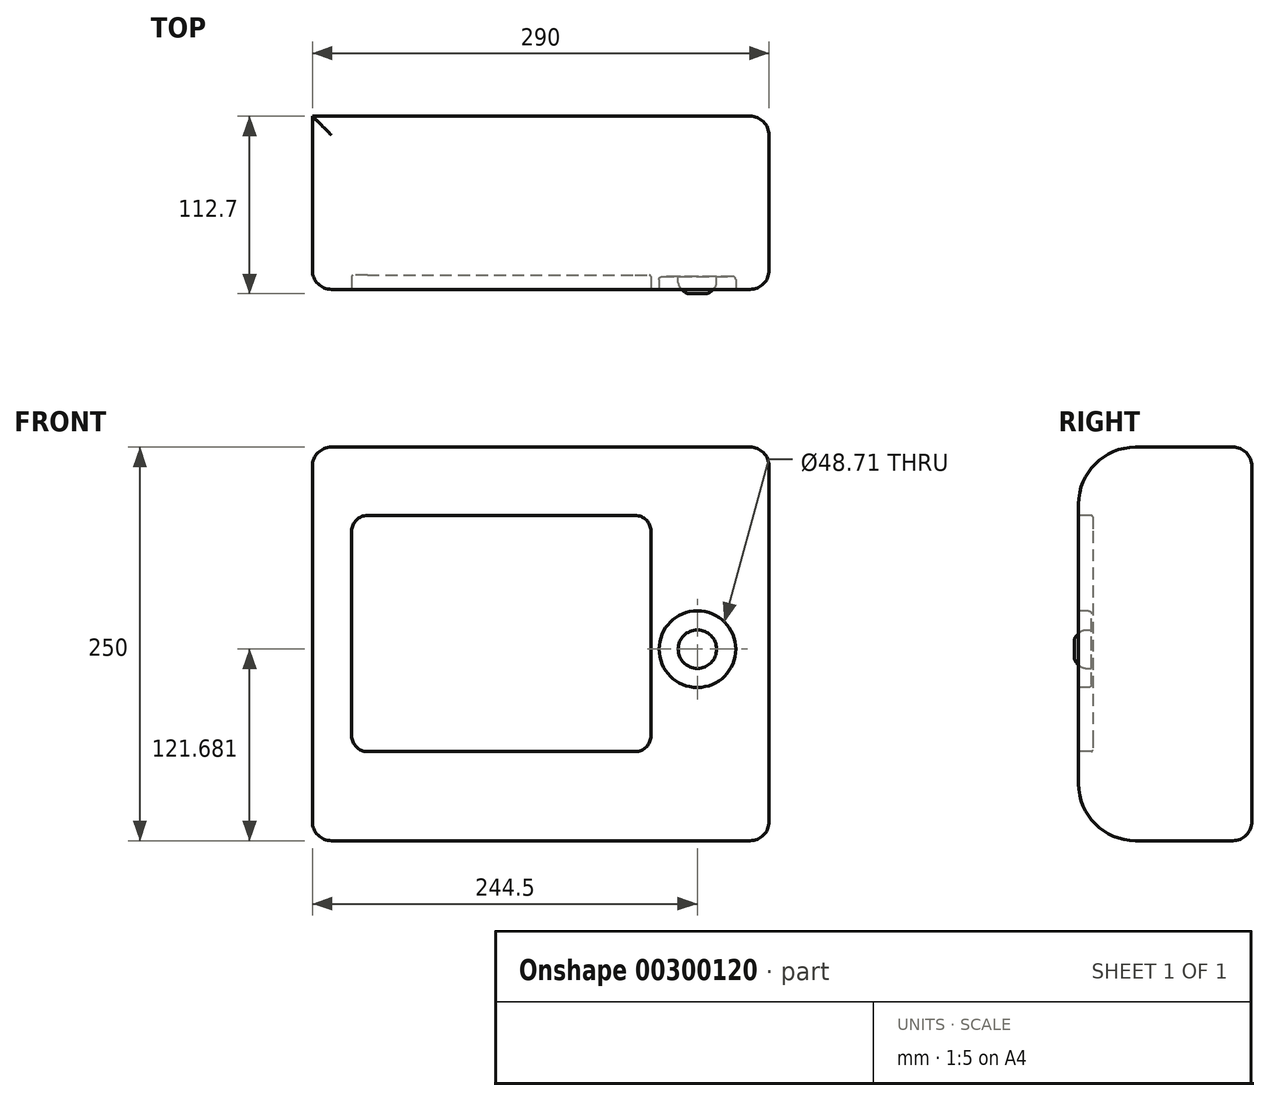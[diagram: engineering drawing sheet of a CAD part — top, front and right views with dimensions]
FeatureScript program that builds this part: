
annotation { "Feature Type Name" : "Feature", "Feature Type Description" : "" }
export const myFeature = defineFeature(function(context is Context, id is Id, definition is map)
    precondition{}
    {
        {
            var Q0;
            Q0=qCreatedBy(makeId("Front.planeOp"),FACE);
            var sketch = newSketch(context, id + "F0", { "sketchPlane" : qUnion([Q0])});
            skLineSegment(sketch, "E0.bottom", {"start": v(-138.87, -70.81) * mm, "end": v(151.13, -70.81) * mm});
            skLineSegment(sketch, "E0.top", {"start": v(-138.87, 179.19) * mm, "end": v(151.13, 179.19) * mm});
            skLineSegment(sketch, "E0.left", {"start": v(-138.87, -70.81) * mm, "end": v(-138.87, 179.19) * mm});
            skLineSegment(sketch, "E0.right", {"start": v(151.13, -70.81) * mm, "end": v(151.13, 179.19) * mm});
            skSolve(sketch);
        }
        {
            var Q0;
            Q0 = qSketchRegion(id + "F0", true);
            extrude(context, id + "F1", {"entities" : qUnion([Q0]), "depth" : 110 * mm});
        }
        {
            var Q0;
            Q0=makeQuery(id+"F1.opExtrude","CAP_EDGE",EDGE,{"disambiguationData":[OSD([sQuery(id+"F0.wireOp",EDGE,"E0.top")])],"isStart":false});
            var Q1;
            Q1=makeQuery(id+"F1.opExtrude","CAP_EDGE",EDGE,{"disambiguationData":[OSD([sQuery(id+"F0.wireOp",EDGE,"E0.bottom")])],"isStart":false});
            fillet(context, id + "F2", {"entities" : qUnion([Q0, Q1]), "radius" : 36.2 * mm, "tangentPropagation" : true, "allowEdgeOverflow" : false});
        }
        {
            var Q0;
            Q0=makeQuery(id+"F1.opExtrude","SWEPT_EDGE",EDGE,{"disambiguationData":[OSD([sQuery(id+"F0.wireOp",EDGE,"E0.top"),sQuery(id+"F0.wireOp",EDGE,"E0.right")])]});
            var Q1;
            Q1=makeQuery(id+"F2.opFillet","BLEND_EDGE",EDGE,{"blendedFrom":[makeQuery(id+"F1.opExtrude","CAP_EDGE",EDGE,{"disambiguationData":[OSD([sQuery(id+"F0.wireOp",EDGE,"E0.top")])],"isStart":false}),makeQuery(id+"F1.opExtrude","SWEPT_FACE",FACE,{"disambiguationData":[OSD([sQuery(id+"F0.wireOp",EDGE,"E0.left")])]})],"blendedInto":[makeQuery(id+"F1.opExtrude","SWEPT_FACE",FACE,{"disambiguationData":[OSD([sQuery(id+"F0.wireOp",EDGE,"E0.left")])]})]});
            var Q2;
            Q2=makeQuery(id+"F1.opExtrude","CAP_EDGE",EDGE,{"disambiguationData":[OSD([sQuery(id+"F0.wireOp",EDGE,"E0.top")])],"isStart":true});
            var Q3;
            Q3=makeQuery(id+"F1.opExtrude","CAP_EDGE",EDGE,{"disambiguationData":[OSD([sQuery(id+"F0.wireOp",EDGE,"E0.right")])],"isStart":true});
            var Q4;
            Q4=makeQuery(id+"F1.opExtrude","CAP_EDGE",EDGE,{"disambiguationData":[OSD([sQuery(id+"F0.wireOp",EDGE,"E0.bottom")])],"isStart":true});
            fillet(context, id + "F3", {"entities" : qUnion([Q0, Q1, Q2, Q3, Q4]), "radius" : 12.07 * mm, "tangentPropagation" : true, "allowEdgeOverflow" : false});
        }
        {
            var Q0;
            Q0=makeQuery(id+"F1.opExtrude","CAP_FACE",FACE,{"disambiguationData":[OSD([sQuery(id+"F0.wireOp",EDGE,"E0.bottom"),sQuery(id+"F0.wireOp",EDGE,"E0.top"),sQuery(id+"F0.wireOp",EDGE,"E0.left"),sQuery(id+"F0.wireOp",EDGE,"E0.right")])],"isStart":false});
            var sketch = newSketch(context, id + "F4", { "sketchPlane" : qUnion([Q0])});
            skCircle(sketch, "E1", {"center": v(105.63, 50.87) * mm, "radius": 24.36 * mm});
            skSolve(sketch);
        }
        {
            var Q0;
            Q0=makeQuery(id+"F4.imprint","IMPRINT",FACE,{"disambiguationData":[TD([[makeQuery(id+"F4.imprint","IMPRINT",EDGE,{"derivedFrom":sQuery(id+"F4.wireOp",EDGE,"E1")}),1.0]])]});
            var Q1;
            Q1=sQuery(id+"F4.wireOp",EDGE,"E1");
            extrude(context, id + "F5", {"entities" : qUnion([Q0]), "operationType" : NewBodyOperationType.REMOVE, "surfaceEntities" : qUnion([Q1]), "oppositeDirection" : true, "depth" : 8.2 * mm});
        }
        {
            var Q0;
            Q0=makeQuery(id+"F5.boolean.opBoolean","COPY",FACE,{"derivedFrom":makeQuery(id+"F5.opExtrude","CAP_FACE",FACE,{"disambiguationData":[OSD([sQuery(id+"F4.wireOp",EDGE,"E1")])],"isStart":false})});
            var sketch = newSketch(context, id + "F6", { "sketchPlane" : qUnion([Q0])});
            skCircle(sketch, "E2", {"center": v(105.63, 50.87) * mm, "radius": 12.21 * mm});
            skSolve(sketch);
        }
        {
            var Q0;
            Q0 = qSketchRegion(id + "F6", true);
            extrude(context, id + "F7", {"entities" : qUnion([Q0]), "operationType" : NewBodyOperationType.ADD, "depth" : 10.9 * mm});
        }
        {
            var Q0;
            Q0=makeQuery(id+"F7.opExtrude","CAP_EDGE",EDGE,{"disambiguationData":[OSD([sQuery(id+"F6.wireOp",EDGE,"E2")])],"isStart":false});
            chamfer(context, id + "F8", {"entities" : qUnion([Q0]), "width" : 5 * mm, "tangentPropagation" : true});
        }
        {
            var Q0;
            {var subQ0=sQuery(id+"F6.wireOp",EDGE,"E2");Q0=makeQuery(id+"F8.opChamfer","BLEND_EDGE",EDGE,{"blendedFrom":[makeQuery(id+"F7.opExtrude","CAP_EDGE",EDGE,{"disambiguationData":[OSD([subQ0])],"isStart":false}),makeQuery(id+"F7.opExtrude","CAP_FACE",FACE,{"disambiguationData":[OSD([subQ0])],"isStart":false})],"blendedInto":[makeQuery(id+"F7.opExtrude","CAP_FACE",FACE,{"disambiguationData":[OSD([subQ0])],"isStart":false})]});}
            var Q1;
            {var subQ0=sQuery(id+"F6.wireOp",EDGE,"E2");Q1=makeQuery(id+"F8.opChamfer","BLEND_EDGE",EDGE,{"blendedFrom":[makeQuery(id+"F7.opExtrude","CAP_EDGE",EDGE,{"disambiguationData":[OSD([subQ0])],"isStart":false}),makeQuery(id+"F7.opExtrude","SWEPT_FACE",FACE,{"disambiguationData":[OSD([subQ0])]})],"blendedInto":[makeQuery(id+"F7.opExtrude","SWEPT_FACE",FACE,{"disambiguationData":[OSD([subQ0])]})]});}
            fillet(context, id + "F9", {"entities" : qUnion([Q0, Q1]), "radius" : 5 * mm, "tangentPropagation" : true, "allowEdgeOverflow" : false});
        }
        {
            var Q0;
            Q0=makeQuery(id+"F7.opExtrude","CAP_EDGE",EDGE,{"disambiguationData":[OSD([sQuery(id+"F6.wireOp",EDGE,"E2")])],"isStart":true});
            var Q1;
            Q1=makeQuery(id+"F5.boolean.opBoolean","COPY",EDGE,{"derivedFrom":makeQuery(id+"F5.opExtrude","CAP_EDGE",EDGE,{"disambiguationData":[OSD([sQuery(id+"F4.wireOp",EDGE,"E1")])],"isStart":false})});
            var Q2;
            Q2=makeQuery(id+"F5.boolean.opBoolean","COPY",EDGE,{"derivedFrom":makeQuery(id+"F5.opExtrude","CAP_EDGE",EDGE,{"disambiguationData":[OSD([sQuery(id+"F4.wireOp",EDGE,"E1")])],"isStart":true})});
            fillet(context, id + "F10", {"entities" : qUnion([Q0, Q1, Q2]), "radius" : 2 * mm, "tangentPropagation" : true, "allowEdgeOverflow" : false});
        }
        {
            var Q0;
            Q0=makeQuery(id+"F1.opExtrude","CAP_FACE",FACE,{"disambiguationData":[OSD([sQuery(id+"F0.wireOp",EDGE,"E0.bottom"),sQuery(id+"F0.wireOp",EDGE,"E0.top"),sQuery(id+"F0.wireOp",EDGE,"E0.left"),sQuery(id+"F0.wireOp",EDGE,"E0.right")])],"isStart":false});
            var sketch = newSketch(context, id + "F11", { "sketchPlane" : qUnion([Q0])});
            skPoint(sketch, "E3.visualSharp", {"position": v(-109.49, 131.68) * mm});
            skLineSegment(sketch, "E4.bottom", {"start": v(-103.92, 135.78) * mm, "end": v(66.08, 135.78) * mm});
            skLineSegment(sketch, "E4.top", {"start": v(-103.92, -14.22) * mm, "end": v(66.08, -14.22) * mm});
            skLineSegment(sketch, "E4.left", {"start": v(-113.92, 125.78) * mm, "end": v(-113.92, -4.22) * mm});
            skLineSegment(sketch, "E4.right", {"start": v(76.08, 125.78) * mm, "end": v(76.08, -4.22) * mm});
            skPoint(sketch, "E5.visualSharp", {"position": v(-113.92, 135.78) * mm});
            skArc(sketch, "E5.filletArc", {"start": v(-103.92, 135.78) * mm, "mid": v(-111, 132.85) * mm, "end": v(-113.92, 125.78) * mm});
            skPoint(sketch, "E6.visualSharp", {"position": v(76.08, 135.78) * mm});
            skArc(sketch, "E6.filletArc", {"start": v(76.08, 125.78) * mm, "mid": v(73.15, 132.85) * mm, "end": v(66.08, 135.78) * mm});
            skPoint(sketch, "E7.visualSharp", {"position": v(-113.92, -14.22) * mm});
            skArc(sketch, "E7.filletArc", {"start": v(-113.92, -4.22) * mm, "mid": v(-111, -11.29) * mm, "end": v(-103.92, -14.22) * mm});
            skPoint(sketch, "E8.visualSharp", {"position": v(76.08, -14.22) * mm});
            skArc(sketch, "E8.filletArc", {"start": v(66.08, -14.22) * mm, "mid": v(73.15, -11.29) * mm, "end": v(76.08, -4.22) * mm});
            skSolve(sketch);
        }
        {
            var Q0;
            Q0 = qSketchRegion(id + "F11", true);
            extrude(context, id + "F12", {"entities" : qUnion([Q0]), "operationType" : NewBodyOperationType.REMOVE, "oppositeDirection" : true, "depth" : 9 * mm});
        }
        {
            var Q0;
            Q0=makeQuery(id+"F12.boolean.opBoolean","COPY",EDGE,{"derivedFrom":makeQuery(id+"F12.opExtrude","CAP_EDGE",EDGE,{"disambiguationData":[OSD([sQuery(id+"F11.wireOp",EDGE,"E7.filletArc")])],"isStart":true})});
            var Q1;
            Q1=makeQuery(id+"F12.boolean.opBoolean","COPY",FACE,{"derivedFrom":makeQuery(id+"F12.opExtrude","CAP_FACE",FACE,{"disambiguationData":[OSD([sQuery(id+"F11.wireOp",EDGE,"E4.bottom"),sQuery(id+"F11.wireOp",EDGE,"E4.top"),sQuery(id+"F11.wireOp",EDGE,"E4.left"),sQuery(id+"F11.wireOp",EDGE,"E4.right"),sQuery(id+"F11.wireOp",EDGE,"E5.filletArc"),sQuery(id+"F11.wireOp",EDGE,"E6.filletArc"),sQuery(id+"F11.wireOp",EDGE,"E7.filletArc"),sQuery(id+"F11.wireOp",EDGE,"E8.filletArc")])],"isStart":false})});
            fillet(context, id + "F13", {"entities" : qUnion([Q0, Q1]), "radius" : 1 * mm, "tangentPropagation" : true, "allowEdgeOverflow" : false});
        }
    });
